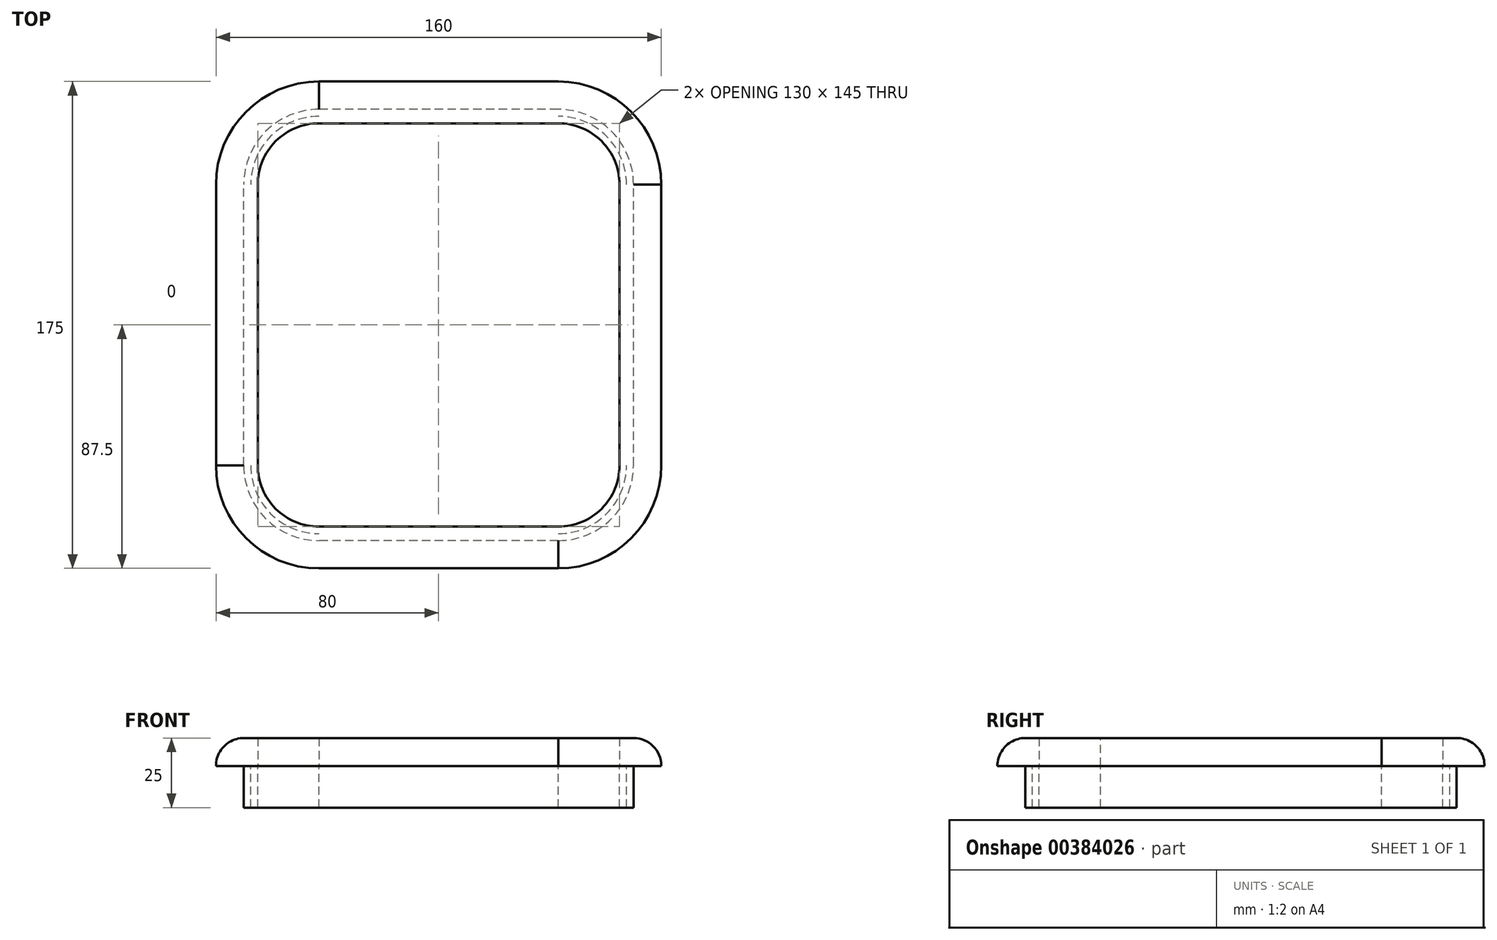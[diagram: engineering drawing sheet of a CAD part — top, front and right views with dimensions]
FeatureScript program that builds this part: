
annotation { "Feature Type Name" : "Feature", "Feature Type Description" : "" }
export const myFeature = defineFeature(function(context is Context, id is Id, definition is map)
    precondition{}
    {
        {
            var Q0;
            Q0=qCreatedBy(makeId("Top.planeOp"),FACE);
            var sketch = newSketch(context, id + "F0", { "sketchPlane" : qUnion([Q0])});
            skLineSegment(sketch, "E0.bottom", {"start": v(43, -77.5) * mm, "end": v(-43, -77.5) * mm});
            skLineSegment(sketch, "E0.top", {"start": v(43, 77.5) * mm, "end": v(-43, 77.5) * mm});
            skLineSegment(sketch, "E0.left", {"start": v(70, -50.5) * mm, "end": v(70, 50.5) * mm});
            skLineSegment(sketch, "E0.right", {"start": v(-70, -50.5) * mm, "end": v(-70, 50.5) * mm});
            skPoint(sketch, "E0.middle", {"position": v(0, 0) * mm});
            skPoint(sketch, "E1.visualSharp", {"position": v(70, 77.5) * mm});
            skArc(sketch, "E1.filletArc", {"start": v(70, 50.5) * mm, "mid": v(62.1, 69.6) * mm, "end": v(43, 77.5) * mm});
            skPoint(sketch, "E2.visualSharp", {"position": v(70, -77.5) * mm});
            skArc(sketch, "E2.filletArc", {"start": v(43, -77.5) * mm, "mid": v(62.1, -69.6) * mm, "end": v(70, -50.5) * mm});
            skPoint(sketch, "E3.visualSharp", {"position": v(-70, -77.5) * mm});
            skArc(sketch, "E3.filletArc", {"start": v(-70, -50.5) * mm, "mid": v(-62.1, -69.6) * mm, "end": v(-43, -77.5) * mm});
            skPoint(sketch, "E4.visualSharp", {"position": v(-70, 77.5) * mm});
            skArc(sketch, "E4.filletArc", {"start": v(-43, 77.5) * mm, "mid": v(-62.1, 69.6) * mm, "end": v(-70, 50.5) * mm});
            skArc(sketch, "E5.0", {"start": v(80, 50.5) * mm, "mid": v(69.16, 76.66) * mm, "end": v(43, 87.5) * mm});
            skLineSegment(sketch, "E5.1", {"start": v(80, -50.5) * mm, "end": v(80, 50.5) * mm});
            skLineSegment(sketch, "E5.2", {"start": v(43, 87.5) * mm, "end": v(-43, 87.5) * mm});
            skArc(sketch, "E5.3", {"start": v(43, -87.5) * mm, "mid": v(69.16, -76.66) * mm, "end": v(80, -50.5) * mm});
            skArc(sketch, "E5.4", {"start": v(-43, 87.5) * mm, "mid": v(-69.16, 76.66) * mm, "end": v(-80, 50.5) * mm});
            skLineSegment(sketch, "E5.5", {"start": v(-80, -50.5) * mm, "end": v(-80, 50.5) * mm});
            skArc(sketch, "E5.6", {"start": v(-80, -50.5) * mm, "mid": v(-69.16, -76.66) * mm, "end": v(-43, -87.5) * mm});
            skLineSegment(sketch, "E5.7", {"start": v(43, -87.5) * mm, "end": v(-43, -87.5) * mm});
            skLineSegment(sketch, "E6.0", {"start": v(65, -50.5) * mm, "end": v(65, 50.5) * mm});
            skArc(sketch, "E6.1", {"start": v(43, -72.5) * mm, "mid": v(58.56, -66.06) * mm, "end": v(65, -50.5) * mm});
            skArc(sketch, "E6.2", {"start": v(65, 50.5) * mm, "mid": v(58.56, 66.06) * mm, "end": v(43, 72.5) * mm});
            skLineSegment(sketch, "E6.3", {"start": v(43, -72.5) * mm, "end": v(-43, -72.5) * mm});
            skLineSegment(sketch, "E6.4", {"start": v(43, 72.5) * mm, "end": v(-43, 72.5) * mm});
            skArc(sketch, "E6.5", {"start": v(-43, 72.5) * mm, "mid": v(-58.56, 66.06) * mm, "end": v(-65, 50.5) * mm});
            skLineSegment(sketch, "E6.6", {"start": v(-65, -50.5) * mm, "end": v(-65, 50.5) * mm});
            skArc(sketch, "E6.7", {"start": v(-65, -50.5) * mm, "mid": v(-58.56, -66.06) * mm, "end": v(-43, -72.5) * mm});
            skSolve(sketch);
        }
        {
            var Q0;
            Q0=makeQuery(id+"F0.imprint","IMPRINT",FACE,{"disambiguationData":[TD([[makeQuery(id+"F0.imprint","IMPRINT",EDGE,{"derivedFrom":sQuery(id+"F0.wireOp",EDGE,"E0.bottom")}),-1.0]])]});
            extrude(context, id + "F1", {"entities" : qUnion([Q0]), "oppositeDirection" : true, "depth" : 15 * mm});
        }
        {
            var Q0;
            Q0 = qSketchRegion(id + "F0", true);
            var Q1;
            Q1=makeQuery(id+"F0.imprint","IMPRINT",FACE,{"disambiguationData":[TD([[makeQuery(id+"F0.imprint","IMPRINT",EDGE,{"derivedFrom":sQuery(id+"F0.wireOp",EDGE,"E0.bottom")}),-1.0]])]});
            extrude(context, id + "F2", {"entities" : qUnion([Q0, Q1]), "depth" : 10 * mm});
        }
        {
            var Q0;
            Q0=makeQuery(id+"F2.opExtrude","CAP_EDGE",EDGE,{"disambiguationData":[OSD([sQuery(id+"F0.wireOp",EDGE,"E5.6")])],"isStart":false});
            fillet(context, id + "F3", {"entities" : qUnion([Q0]), "radius" : 10 * mm, "tangentPropagation" : true, "allowEdgeOverflow" : false});
        }
        {
            var Q0;
            Q0=makeQuery(id+"F1.opExtrude","CAP_FACE",FACE,{"disambiguationData":[OSD([sQuery(id+"F0.wireOp",EDGE,"E0.bottom"),sQuery(id+"F0.wireOp",EDGE,"E0.top"),sQuery(id+"F0.wireOp",EDGE,"E0.left"),sQuery(id+"F0.wireOp",EDGE,"E0.right"),sQuery(id+"F0.wireOp",EDGE,"E1.filletArc"),sQuery(id+"F0.wireOp",EDGE,"E2.filletArc"),sQuery(id+"F0.wireOp",EDGE,"E3.filletArc"),sQuery(id+"F0.wireOp",EDGE,"E4.filletArc")])],"isStart":false});
            var Q1;
            Q1=makeQuery(id+"F1.opExtrude","CAP_FACE",FACE,{"disambiguationData":[OSD([sQuery(id+"F0.wireOp",EDGE,"E0.bottom"),sQuery(id+"F0.wireOp",EDGE,"E0.top"),sQuery(id+"F0.wireOp",EDGE,"E0.left"),sQuery(id+"F0.wireOp",EDGE,"E0.right"),sQuery(id+"F0.wireOp",EDGE,"E1.filletArc"),sQuery(id+"F0.wireOp",EDGE,"E2.filletArc"),sQuery(id+"F0.wireOp",EDGE,"E3.filletArc"),sQuery(id+"F0.wireOp",EDGE,"E4.filletArc")])],"isStart":true});
            shell(context, id + "F4", {"entities" : qUnion([Q0, Q1]), "thickness" : 2.5 * mm});
        }
    });
